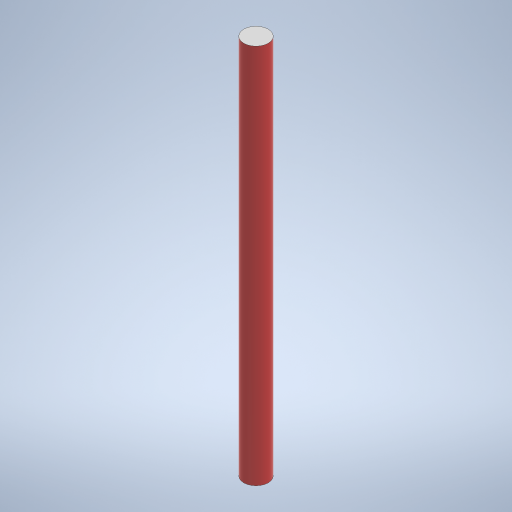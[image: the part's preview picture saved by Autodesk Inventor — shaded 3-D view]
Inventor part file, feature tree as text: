
AUTODESK INVENTOR PART (.ipt)
format: ipt  version: 2023 (Build 270158000, 158)  size: 230,912 bytes
history: native  units: mm
features: extrude x1, sketch x1
ambient origin geometry x8: Origin, YZ Plane, XZ Plane, XY Plane, X Axis, Y Axis, Z Axis, Center Point
bodies: Solid1 (feature_tree)
feature tree (2):
  extrude  "Extrusion1"  Depth=155.5mm TaperAngle=0.0deg
  sketch  "Sketch1"  dims[d0=10.0mm d1=155.5mm d2=0.0mm]
